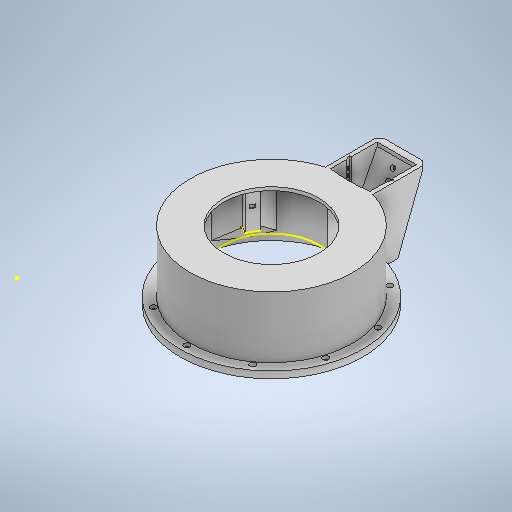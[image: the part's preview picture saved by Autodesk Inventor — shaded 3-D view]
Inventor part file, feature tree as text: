
AUTODESK INVENTOR PART (.ipt)
format: ipt  version: 2025.2 (Build 292293000, 293)  size: 1,971,712 bytes
history: native  units: in
note: dims shown in document units (in); Inventor stores cm internally (conversion verified against a paired STEP export)
features: sketch x54, extrude x51, plane x24, projected_geometry x20, other x3, chamfer x2
ambient origin geometry x8: Origin, YZ Plane, XZ Plane, XY Plane, X Axis, Y Axis, Z Axis, Center Point
bodies: Body1 (feature_tree)
feature tree (154):
  other  "Cylinder.ipt"
  extrude  "Extrusion1"  Depth=0.3937in
  extrude  "Extrusion2"  Depth=0.3937in TaperAngle=0.0deg
  sketch  "Sketch3"  dims[d7=11.2205in d8=10.6299in]
  extrude  "Extrusion3"  Depth=10.6299in
  extrude  "Extrusion5"  Depth=0.1969in TaperAngle=0.0deg
  sketch  "Sketch6"  dims[d36=10.6299in d46=9.065in]
  extrude  "Extrusion6"  Depth=10.6299in
  extrude  "Extrusion7"  TaperAngle=0.0deg  [1 undecoded]
  extrude  "Extrusion8"  Depth=2.1654in
  plane  "Work Plane1"
  extrude  "Extrusion9"  Depth=10.6299in
  extrude  "Extrusion21"  Depth=0.3937in
  sketch  "Sketch19"  dims[d164=1.5298in d165=0.0787in]
  extrude  "Extrusion34"  Depth=2.5591in
  extrude  "Extrusion53"  Depth=0.5433in
  plane  "Work Plane2"
  plane  "Work Plane3"
  plane  "Work Plane5"
  plane  "Work Plane6"
  extrude  "Extrusion88"  Depth=0.0787in
  extrude  "Extrusion89"  Depth=0.0787in
  extrude  "Extrusion91"  TaperAngle=90.0deg  [1 undecoded]
  plane  "Work Plane7"
  plane  "Work Plane8"
  plane  "Work Plane9"
  plane  "Work Plane10"
  extrude  "Extrusion102"  Depth=0.0787in
  plane  "Work Plane11"
  plane  "Work Plane12"
  extrude  "Extrusion108"  Depth=0.3425in
  plane  "Work Plane13"
  extrude  "bracket"  Depth=10.4151in
  plane  "Work Plane14"
  extrude  "Extrusion120"  Depth=0.5433in
  extrude  "Extrusion121"  Depth=3.5433in
  extrude  "Extrusion122"  Depth=2.7608in
  extrude  "bracketwalls"  [1 undecoded]
  extrude  "name"  Depth=0.0591in
  plane  "Work Plane16"
  plane  "Work Plane15"
  plane  "Work Plane17"
  extrude  "Extrusion137"  Depth=2.3622in
  plane  "Work Plane18"
  extrude  "Extrusion139"  Depth=0.3937in
  extrude  "Extrusion140"  Depth=0.1772in
  extrude  "Extrusion141"  Depth=1.1811in TaperAngle=0.0deg
  plane  "Work Plane20"
  sketch  "Sketch136"  dims[d607=3.3465in d608=0.0in d609=0.7874in d610=0.0in]
  plane  "Work Plane21"
  extrude  "Extrusion147"  Depth=3.3661in TaperAngle=0.0deg
  extrude  "Extrusion148"  TaperAngle=120.0deg  [1 undecoded]
  extrude  "Extrusion152"  Depth=2.7559in TaperAngle=0.0deg
  extrude  "Extrusion153"  Depth=0.7874in TaperAngle=0.0deg
  extrude  "Extrusion157"  Depth=0.7874in
  extrude  "Extrusion158"  Depth=0.1575in TaperAngle=0.0deg
  extrude  "Extrusion159"  Depth=0.1969in TaperAngle=0.0deg
  chamfer  "Chamfer25"  Distance=0.1969in
  extrude  "Extrusion160"  Depth=0.1969in TaperAngle=0.0deg
  extrude  "Extrusion161"  TaperAngle=0.0deg  [1 undecoded]
  extrude  "Extrusion162"  Depth=0.3937in
  plane  "Work Plane19"
  sketch  "Sketch155"  dims[d738=3.937in d739=0.5512in d740=0.0in]
  extrude  "Extrusion163"  Depth=0.2362in
  extrude  "Extrusion164"  Depth=0.2362in
  extrude  "Extrusion165"  Depth=3.7598in TaperAngle=0.0deg
  extrude  "Extrusion166"  Depth=0.7609in
  chamfer  "Chamfer26"  Distance=0.5512in
  extrude  "Extrusion167"  Depth=0.1969in TaperAngle=0.0deg
  plane  "Work Plane25"
  plane  "Work Plane22"
  plane  "Work Plane23"
  plane  "Work Plane24"
  extrude  "Extrusion177"  Depth=0.1969in TaperAngle=0.0deg
  extrude  "Extrusion178"  Depth=2.2835in TaperAngle=0.0deg
  extrude  "Extrusion179"  Depth=0.5906in
  extrude  "Extrusion180"  Depth=0.2756in
  extrude  "Extrusion181"  TaperAngle=0.0deg  [1 undecoded]
  extrude  "Extrusion182"  Depth=0.5512in
  extrude  "Extrusion183"  Depth=0.315in TaperAngle=0.0deg
  extrude  "Extrusion184"  Depth=0.3937in TaperAngle=0.0deg
  extrude  "Extrusion185"  Depth=0.2362in TaperAngle=45.0deg
  sketch  "Sketch173"  dims[d783=0.7874in d785=120.0deg]
  extrude  "Extrusion186"  Depth=0.7874in TaperAngle=90.0deg
  other  "Solid12::Cylinder.ipt"
  other  "TaggingFeature1"
  sketch  "Sketch1"  dims[d0=0.3937in d2=10.2362in]
  sketch  "Sketch2"  dims[d3=0.0in d4=0.0in d5=0.3937in d6=0.0in]
  sketch  "Sketch5"  dims[d24=0.1969in d25=0.0in d31=0.0in d32=0.0in]
  sketch  "Sketch7"  dims[d107=2.2047in d108=0.0in d113=2.5591in]
  sketch  "Sketch9"  dims[d117=0.0591in d120=0.5433in]
  sketch  "Sketch14"  dims[d122=9.4488in d134=0.0787in]
  sketch  "Sketch22"  dims[d166=1.8325in d167=90.0deg]
  sketch  "Sketch Circular Pattern3"  dims[d10=0.1969in d11=0.0in d15=0.1969in d16=0.0in]
  sketch  "Sketch76"  dims[d173=1.1614in d174=0.0in d175=0.0787in]
  sketch  "Sketch77"  dims[d209=0.2165in d210=0.3425in]
  sketch  "Sketch79"  dims[d211=3.937in d213=360.0deg d217=10.4151in]
  sketch  "Sketch93"  dims[d218=9.065in d223=0.5433in]
  sketch  "Sketch99"  dims[d224=1.8228in d225=3.5433in]
  sketch  "Sketch104"  dims[d226=2.564in d227=2.7608in]
  sketch  "Sketch111"  dims[d228=3.5433in d269=-3.5433in]
  sketch  "Sketch112"  dims[d306=4.5276in d307=0.0591in]
  sketch  "Sketch113"  dims[d308=2.7608in d309=2.3622in]
  projected_geometry  "Projected Loop4"
  projected_geometry  "Projected Loop5"
  sketch  "Sketch120"  dims[d313=3.3661in d314=0.3937in d315=0.0in d316=0.0in d452=0.1772in]
  projected_geometry  "Projected Loop10"
  projected_geometry  "Projected Loop11"
  sketch  "Sketch122"  dims[d453=0.3396in d454=0.1772in]
  sketch  "Sketch130"  dims[d455=0.3396in d489=1.1811in d490=0.0in]
  sketch  "Sketch132"  dims[d491=3.3661in d492=0.3937in d493=0.0in d494=0.0in d497=3.3661in d498=0.0in]
  projected_geometry  "Projected Loop15"
  sketch  "Sketch133"  dims[d548=3.3465in d549=0.0in d554=120.0deg]
  sketch  "Sketch134"  dims[d563=2.7559in d564=0.0in d579=2.7559in d580=0.0in]
  sketch  "Sketch139"  dims[d611=3.3465in d612=0.0in d626=0.7874in]
  sketch  "Sketch140"  dims[d635=1.4961in d636=0.0in d646=0.1575in d647=0.0in]
  projected_geometry  "Projected Loop17"
  sketch  "Sketch144"  dims[d675=2.2835in d676=0.0in d679=0.1683in d680=0.0in d681=0.1969in d682=0.0in]
  sketch  "Sketch145"  dims[d683=5.5413in d684=0.1969in d685=0.0in]
  sketch  "Sketch149"  dims[d692=6.378in d693=0.2805in d703=0.0in d704=0.0in]
  projected_geometry  "Projected Loop20"
  sketch  "Sketch150"  dims[d705=0.3937in d706=0.0in d719=1.1417in]
  sketch  "Sketch151"  dims[d720=1.1417in d721=0.2362in]
  projected_geometry  "Projected Loop21"
  sketch  "Sketch152"  dims[d722=0.2362in d723=0.2362in]
  sketch  "Sketch153"  dims[d724=0.0in d725=0.0in d726=3.7598in d727=0.0in]
  sketch  "Sketch154"  dims[d733=0.4329in d737=0.7609in]
  sketch  "Sketch156"  dims[d741=0.0in d742=0.0in d746=0.1969in d747=0.0in]
  sketch  "Sketch157"  dims[d748=0.1969in d749=0.0787in d750=45.0deg d751=0.9055in d752=0.0in]
  sketch  "Sketch158"  dims[d753=0.1969in d754=2.2835in d755=0.0in]
  projected_geometry  "Projected Loop22"
  sketch  "Sketch Circular Pattern4"  dims[d17=10.6299in d18=0.2953in]
  sketch  "Sketch Circular Pattern5"  dims[d33=2.1654in d34=0.0in d35=9.8425in]
  sketch  "Sketch Circular Pattern6"  dims[d47=0.3937in d48=0.0in d88=0.0787in]
  sketch  "Sketch165"  dims[d756=0.2756in d757=0.5906in]
  sketch  "Sketch166"  dims[d758=1.1417in d759=0.2756in]
  projected_geometry  "Projected Loop39"
  projected_geometry  "Projected Loop40"
  sketch  "Sketch167"  dims[d760=0.5906in d761=0.0in d762=0.0in]
  sketch  "Sketch168"  dims[d763=-0.5906in d764=0.5512in]
  sketch  "Sketch169"  dims[d765=0.5512in d766=0.315in d767=0.0in]
  projected_geometry  "Projected Loop41"
  projected_geometry  "Projected Loop42"
  projected_geometry  "Projected Loop43"
  sketch  "Sketch170"  dims[d768=0.3937in d769=0.0in d770=0.3937in d771=0.0in]
  projected_geometry  "Projected Loop44"
  sketch  "Sketch171"  dims[d772=0.0in d773=0.0in d774=0.2362in d775=0.0787in d776=45.0deg]
  projected_geometry  "Projected Loop45"
  sketch  "Sketch172"  dims[d777=0.2165in d778=0.0in d779=0.7874in d781=90.0deg]
  projected_geometry  "Projected Loop46"
  projected_geometry  "Projected Loop47"
  projected_geometry  "Projected Loop48"
  projected_geometry  "Projected Loop49"
  sketch  "Sketch174"  dims[d787=0.7874in d789=120.0deg d824=0.1181in d825=1.9685in d826=0.0in d827=0.7874in d828=0.0in d829=0.7874in d830=0.0in d831=0.1969in d832=0.0in d833=0.1969in d834=0.7874in d835=0.0in d836=0.0in d837=0.1969in d838=0.0in d839=0.0in d840=0.3436in d841=0.0in d842=0.3436in d843=0.0in d844=0.3436in d845=1.9685in d846=0.0in d847=7.0079in d143=0.0197in d144=0.0344in d145=0.0197in d146=0.0344in d153=0.0in d154=0.0in d155=0.0in d156=0.0in d201=0.0197in d202=0.0344in d203=0.0197in d204=0.0344in d215=0.0197in d216=0.0344in d294=0.0197in d295=0.0344in d296=0.0197in d297=0.0344in d330=0.0197in d331=0.0344in d332=0.0197in d333=0.0344in d419=0.0197in d420=0.0344in d421=0.0197in d422=0.0344in d423=0.0344in d424=0.0197in d425=0.0344in d505=0.0197in d506=0.0344in d507=0.0197in d508=0.0344in d514=0.0197in d515=0.0344in d516=0.0197in d517=0.0344in d546=0.0197in d547=0.0344in d555=0.0197in d556=0.0344in d557=0.0197in d558=0.0344in d588=0.0197in d589=0.0344in d590=0.0197in d591=0.0344in d617=0.0197in d618=0.0344in d619=0.0197in d620=0.0344in d628=0.0197in d629=0.0344in d630=0.0197in d631=0.0344in d648=0.0197in d649=0.0344in d669=0.0197in d670=0.0344in d671=0.0197in d672=0.0344in d793=0.0197in d794=0.0344in d795=0.0197in d796=0.0344in]
note: 6 required parameter values undecoded (feature->parameter linkage not recoverable at this tier; creation-order binding heuristic only, values carry confidence <= 0.55)
